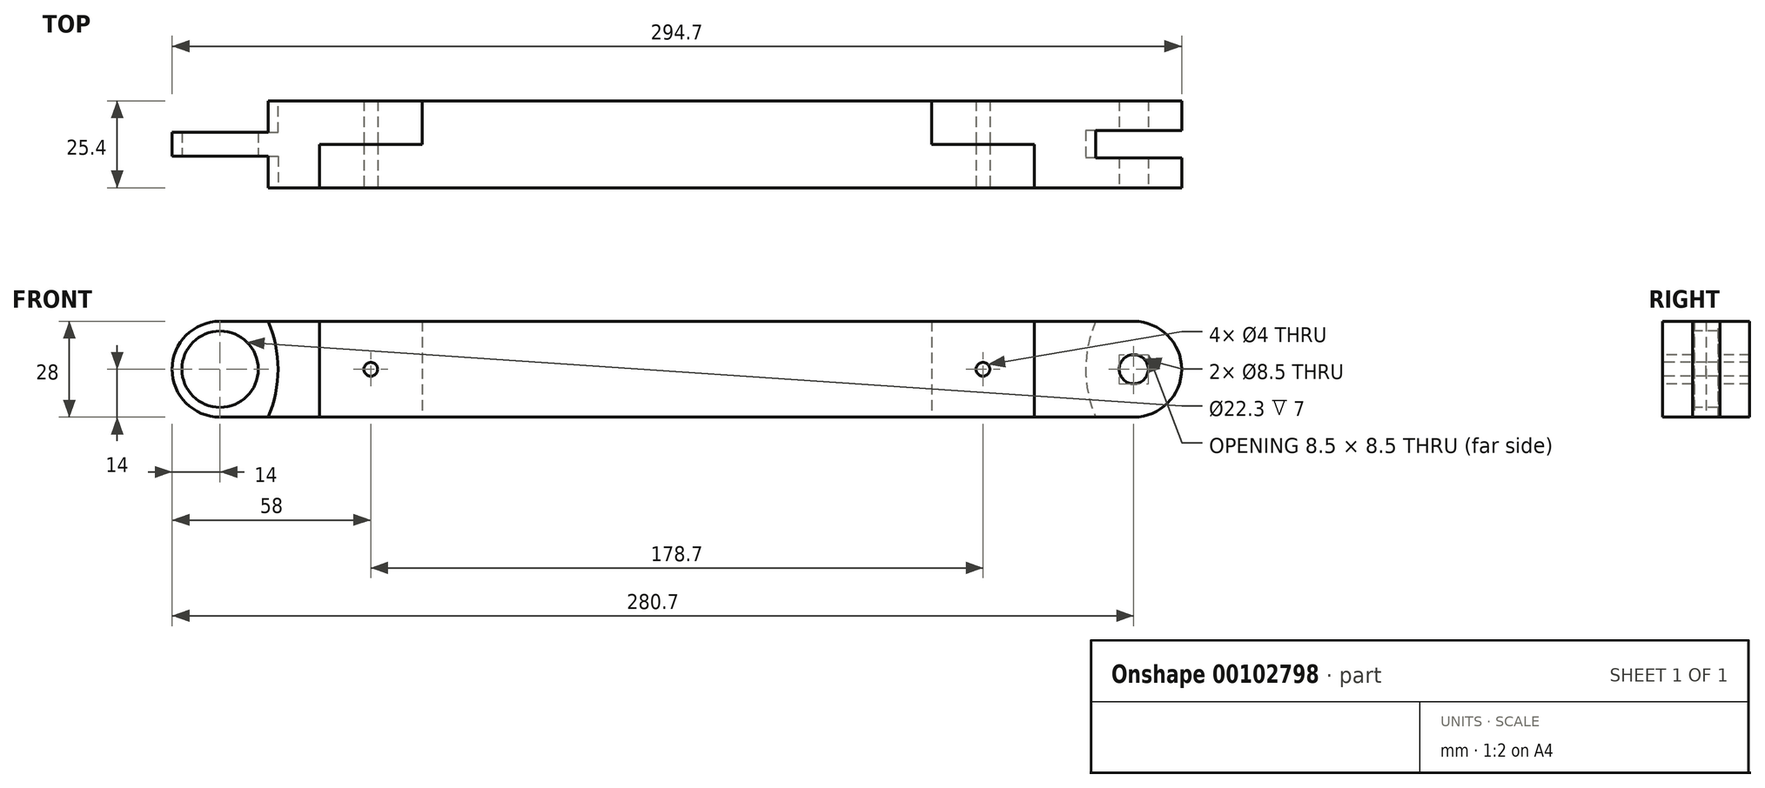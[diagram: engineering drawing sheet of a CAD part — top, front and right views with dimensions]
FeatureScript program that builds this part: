
annotation { "Feature Type Name" : "Feature", "Feature Type Description" : "" }
export const myFeature = defineFeature(function(context is Context, id is Id, definition is map)
    precondition{}
    {
        {
            assignVariable(context, id + "F0", {"name" : "diameter", "anyValue" : 28});
        }
        {
            var Q0;
            Q0=qCreatedBy(makeId("Top.planeOp"),FACE);
            var sketch = newSketch(context, id + "F1", { "sketchPlane" : qUnion([Q0])});
            skLineSegment(sketch, "E0", {"start": v(-133.35, 12.7) * mm, "end": v(133.35, 12.7) * mm});
            skLineSegment(sketch, "E1", {"start": v(133.35, 12.7) * mm, "end": v(133.35, 4) * mm});
            skLineSegment(sketch, "E2", {"start": v(133.35, 4) * mm, "end": v(105.35, 4) * mm});
            skLineSegment(sketch, "E3", {"start": v(105.35, 4) * mm, "end": v(105.35, -4) * mm});
            skLineSegment(sketch, "E4", {"start": v(105.35, -4) * mm, "end": v(133.35, -4) * mm});
            skLineSegment(sketch, "E5", {"start": v(133.35, -4) * mm, "end": v(133.35, -12.7) * mm});
            skLineSegment(sketch, "E6", {"start": v(133.35, -12.7) * mm, "end": v(-133.35, -12.7) * mm});
            skLineSegment(sketch, "E7", {"start": v(-133.35, -12.7) * mm, "end": v(-133.35, -3.5) * mm});
            skLineSegment(sketch, "E8", {"start": v(-133.35, -3.5) * mm, "end": v(-161.35, -3.5) * mm});
            skLineSegment(sketch, "E9", {"start": v(-161.35, -3.5) * mm, "end": v(-161.35, 3.5) * mm});
            skLineSegment(sketch, "E10", {"start": v(-161.35, 3.5) * mm, "end": v(-133.35, 3.5) * mm});
            skLineSegment(sketch, "E11", {"start": v(-133.35, 3.5) * mm, "end": v(-133.35, 12.7) * mm});
            skPoint(sketch, "E12", {"position": v(-147.35, 0) * mm});
            skPoint(sketch, "E12.positionSnap0", {"position": v(-161.35, 0) * mm});
            skPoint(sketch, "E12.positionSnap1", {"position": v(-147.35, 3.5) * mm});
            skPoint(sketch, "E13", {"position": v(119.35, 0) * mm});
            skPoint(sketch, "E13.positionSnap0", {"position": v(105.35, 0) * mm});
            skPoint(sketch, "E13.positionSnap1", {"position": v(119.35, 4) * mm});
            skPoint(sketch, "E14", {"position": v(0, 0) * mm});
            skPoint(sketch, "E14.positionSnap0", {"position": v(0, 12.7) * mm});
            skLineSegment(sketch, "E15", {"start": v(-118.35, -12.7) * mm, "end": v(-118.35, 0) * mm});
            skLineSegment(sketch, "E16", {"start": v(-118.35, 0) * mm, "end": v(-88.35, 0) * mm});
            skLineSegment(sketch, "E17", {"start": v(-88.35, 0) * mm, "end": v(-88.35, 12.7) * mm});
            skLineSegment(sketch, "E18", {"start": v(0, 12.7) * mm, "end": v(0, -12.7) * mm, "construction": true});
            skLineSegment(sketch, "E19", {"start": v(90.35, -12.7) * mm, "end": v(90.35, 0) * mm});
            skLineSegment(sketch, "E20", {"start": v(90.35, 0) * mm, "end": v(60.35, 0) * mm});
            skLineSegment(sketch, "E21", {"start": v(60.35, 0) * mm, "end": v(60.35, 12.7) * mm});
            skLineSegment(sketch, "E22", {"start": v(-133.35, -8.1) * mm, "end": v(-118.35, -8.1) * mm, "construction": true});
            skLineSegment(sketch, "E23", {"start": v(90.35, 0) * mm, "end": v(105.35, 0) * mm, "construction": true});
            skSolve(sketch);
        }
        {
            var Q0;
            {var subQ1=sQuery(id+"F1.wireOp",EDGE,"E7");Q0=makeQuery(id+"F1.imprint","IMPRINT",FACE,{"disambiguationData":[TD([[makeQuery(id+"F1.imprint","IMPRINT",EDGE,{"derivedFrom":subQ1}),-1.0]])]});}
            extrude(context, id + "F2", {"entities" : qUnion([Q0]), "depth" : (getVariable(context, 'diameter')) * mm});
        }
        {
            var Q0;
            {var subQ0=sQuery(id+"F1.wireOp",EDGE,"E15");Q0=makeQuery(id+"F1.imprint","IMPRINT",FACE,{"disambiguationData":[TD([[makeQuery(id+"F1.imprint","IMPRINT",EDGE,{"derivedFrom":subQ0}),-1.0]])]});}
            var Q1;
            Q1=makeQuery(id+"F2.opExtrude","CAP_FACE",FACE,{"disambiguationData":[OSD([sQuery(id+"F1.wireOp",EDGE,"E0"),sQuery(id+"F1.wireOp",EDGE,"E6"),sQuery(id+"F1.wireOp",EDGE,"E7"),sQuery(id+"F1.wireOp",EDGE,"E8"),sQuery(id+"F1.wireOp",EDGE,"E9"),sQuery(id+"F1.wireOp",EDGE,"E10"),sQuery(id+"F1.wireOp",EDGE,"E11"),sQuery(id+"F1.wireOp",EDGE,"E15"),sQuery(id+"F1.wireOp",EDGE,"E16"),sQuery(id+"F1.wireOp",EDGE,"E17")])],"isStart":false});
            extrude(context, id + "F3", {"entities" : qUnion([Q0]), "endBound" : BoundingType.UP_TO_SURFACE, "endBoundEntityFace" : qUnion([Q1]), "depth" : 25 * mm});
        }
        {
            var Q0;
            {var subQ0=sQuery(id+"F1.wireOp",EDGE,"E1");Q0=makeQuery(id+"F1.imprint","IMPRINT",FACE,{"disambiguationData":[TD([[makeQuery(id+"F1.imprint","IMPRINT",EDGE,{"derivedFrom":subQ0}),-1.0]])]});}
            var Q1;
            Q1=makeQuery(id+"F2.opExtrude","CAP_FACE",FACE,{"disambiguationData":[OSD([sQuery(id+"F1.wireOp",EDGE,"E0"),sQuery(id+"F1.wireOp",EDGE,"E6"),sQuery(id+"F1.wireOp",EDGE,"E7"),sQuery(id+"F1.wireOp",EDGE,"E8"),sQuery(id+"F1.wireOp",EDGE,"E9"),sQuery(id+"F1.wireOp",EDGE,"E10"),sQuery(id+"F1.wireOp",EDGE,"E11"),sQuery(id+"F1.wireOp",EDGE,"E15"),sQuery(id+"F1.wireOp",EDGE,"E16"),sQuery(id+"F1.wireOp",EDGE,"E17")])],"isStart":false});
            extrude(context, id + "F4", {"entities" : qUnion([Q0]), "endBound" : BoundingType.UP_TO_SURFACE, "endBoundEntityFace" : qUnion([Q1]), "depth" : 25 * mm});
        }
        {
            var Q0;
            Q0=makeQuery(id+"F3.opExtrude","SWEPT_FACE",FACE,{"disambiguationData":[OSD([sQuery(id+"F1.wireOp",EDGE,"E6")])]});
            var sketch = newSketch(context, id + "F5", { "sketchPlane" : qUnion([Q0])});
            skLineSegment(sketch, "E24.0.0", {"start": v(-161.35, 0) * mm, "end": v(-133.35, 0) * mm});
            skLineSegment(sketch, "E24.0.1", {"start": v(-133.35, 0) * mm, "end": v(-133.35, 28) * mm});
            skLineSegment(sketch, "E24.0.2", {"start": v(-133.35, 28) * mm, "end": v(-161.35, 28) * mm});
            skLineSegment(sketch, "E24.0.3", {"start": v(-161.35, 28) * mm, "end": v(-161.35, 0) * mm});
            skLineSegment(sketch, "E25.0.0", {"start": v(105.35, 0) * mm, "end": v(105.35, 28) * mm});
            skLineSegment(sketch, "E25.0.1", {"start": v(105.35, 28) * mm, "end": v(133.35, 28) * mm});
            skLineSegment(sketch, "E25.0.2", {"start": v(133.35, 28) * mm, "end": v(133.35, 0) * mm});
            skLineSegment(sketch, "E25.0.3", {"start": v(133.35, 0) * mm, "end": v(105.35, 0) * mm});
            skCircle(sketch, "E26", {"center": v(119.35, 14) * mm, "radius": 4.25 * mm});
            skPoint(sketch, "E26.centerSnap0", {"position": v(133.35, 14) * mm});
            skPoint(sketch, "E26.centerSnap1", {"position": v(119.35, 28) * mm});
            skArc(sketch, "E27", {"start": v(119.35, 28) * mm, "mid": v(133.35, 14) * mm, "end": v(119.35, 0) * mm});
            skArc(sketch, "E28", {"start": v(108.27, 28) * mm, "mid": v(105.35, 14) * mm, "end": v(108.27, 0) * mm});
            skCircle(sketch, "E29", {"center": v(-147.35, 14) * mm, "radius": 11.15 * mm});
            skPoint(sketch, "E29.centerSnap0", {"position": v(-161.35, 14) * mm});
            skPoint(sketch, "E29.centerSnap1", {"position": v(-147.35, 28) * mm});
            skArc(sketch, "E30", {"start": v(-147.35, 28) * mm, "mid": v(-161.35, 14) * mm, "end": v(-147.35, 0) * mm});
            skArc(sketch, "E31", {"start": v(-133.35, 28) * mm, "mid": v(-130.43, 14) * mm, "end": v(-133.35, 0) * mm});
            skSolve(sketch);
        }
        {
            var Q0;
            Q0=makeQuery(id+"F5.imprint","IMPRINT",FACE,{"disambiguationData":[TD([[makeQuery(id+"F5.imprint","IMPRINT",EDGE,{"derivedFrom":sQuery(id+"F5.wireOp",EDGE,"E29")}),1.0]])]});
            var Q1;
            {var subQ0=sQuery(id+"F5.wireOp",EDGE,"E24.0.3");var subQ1=sQuery(id+"F5.wireOp",EDGE,"E24.0.2");var subQ2=makeQuery(id+"F5.imprint","INTERSECT",VERTEX,{"derivedFrom":[subQ1,subQ0]});Q1=makeQuery(id+"F5.imprint","IMPRINT",FACE,{"disambiguationData":[TD([[makeQuery(id+"F5.imprint","IMPRINT",EDGE,{"disambiguationData":[TD([[subQ2,1.0]])],"derivedFrom":subQ1}),1.0]])]});}
            var Q2;
            {var subQ0=sQuery(id+"F5.wireOp",EDGE,"E24.0.3");var subQ1=sQuery(id+"F5.wireOp",EDGE,"E24.0.0");var subQ2=makeQuery(id+"F5.imprint","INTERSECT",VERTEX,{"derivedFrom":[subQ1,subQ0]});Q2=makeQuery(id+"F5.imprint","IMPRINT",FACE,{"disambiguationData":[TD([[makeQuery(id+"F5.imprint","IMPRINT",EDGE,{"disambiguationData":[TD([[subQ2,-1.0]])],"derivedFrom":subQ1}),1.0]])]});}
            var Q3;
            Q3=makeQuery(id+"F2.opExtrude","SWEPT_FACE",FACE,{"disambiguationData":[OSD([sQuery(id+"F1.wireOp",EDGE,"E10")])]});
            extrude(context, id + "F6", {"entities" : qUnion([Q0, Q1, Q2]), "operationType" : NewBodyOperationType.REMOVE, "endBound" : BoundingType.UP_TO_SURFACE, "oppositeDirection" : true, "endBoundEntityFace" : qUnion([Q3]), "depth" : 25 * mm});
        }
        {
            var Q0;
            Q0=makeQuery(id+"F5.imprint","IMPRINT",FACE,{"disambiguationData":[TD([[makeQuery(id+"F5.imprint","IMPRINT",EDGE,{"derivedFrom":sQuery(id+"F5.wireOp",EDGE,"E26")}),1.0]])]});
            var Q1;
            {var subQ0=sQuery(id+"F5.wireOp",EDGE,"E25.0.2");var subQ1=sQuery(id+"F5.wireOp",EDGE,"E25.0.1");var subQ2=makeQuery(id+"F5.imprint","INTERSECT",VERTEX,{"derivedFrom":[subQ1,subQ0]});Q1=makeQuery(id+"F5.imprint","IMPRINT",FACE,{"disambiguationData":[TD([[makeQuery(id+"F5.imprint","IMPRINT",EDGE,{"disambiguationData":[TD([[subQ2,1.0]])],"derivedFrom":subQ1}),-1.0]])]});}
            var Q2;
            {var subQ0=sQuery(id+"F5.wireOp",EDGE,"E25.0.3");var subQ1=sQuery(id+"F5.wireOp",EDGE,"E25.0.2");var subQ2=makeQuery(id+"F5.imprint","INTERSECT",VERTEX,{"derivedFrom":[subQ1,subQ0]});Q2=makeQuery(id+"F5.imprint","IMPRINT",FACE,{"disambiguationData":[TD([[makeQuery(id+"F5.imprint","IMPRINT",EDGE,{"disambiguationData":[TD([[subQ2,1.0]])],"derivedFrom":subQ1}),-1.0]])]});}
            var Q3;
            Q3=makeQuery(id+"F4.opExtrude","SWEPT_FACE",FACE,{"disambiguationData":[OSD([sQuery(id+"F1.wireOp",EDGE,"E0")])]});
            extrude(context, id + "F7", {"entities" : qUnion([Q0, Q1, Q2]), "operationType" : NewBodyOperationType.REMOVE, "endBound" : BoundingType.UP_TO_SURFACE, "oppositeDirection" : true, "endBoundEntityFace" : qUnion([Q3]), "depth" : 25 * mm});
        }
        {
            var Q0;
            {var subQ0=sQuery(id+"F5.wireOp",EDGE,"E25.0.1");var subQ1=sQuery(id+"F5.wireOp",EDGE,"E25.0.0");var subQ2=makeQuery(id+"F5.imprint","INTERSECT",VERTEX,{"derivedFrom":[subQ1,subQ0]});Q0=makeQuery(id+"F5.imprint","IMPRINT",FACE,{"disambiguationData":[TD([[makeQuery(id+"F5.imprint","IMPRINT",EDGE,{"disambiguationData":[TD([[subQ2,1.0]])],"derivedFrom":subQ1}),-1.0]])]});}
            var Q1;
            {var subQ0=sQuery(id+"F5.wireOp",EDGE,"E25.0.3");var subQ1=sQuery(id+"F5.wireOp",EDGE,"E25.0.0");var subQ2=makeQuery(id+"F5.imprint","INTERSECT",VERTEX,{"derivedFrom":[subQ1,subQ0]});Q1=makeQuery(id+"F5.imprint","IMPRINT",FACE,{"disambiguationData":[TD([[makeQuery(id+"F5.imprint","IMPRINT",EDGE,{"disambiguationData":[TD([[subQ2,-1.0]])],"derivedFrom":subQ1}),-1.0]])]});}
            var Q2;
            Q2=makeQuery(id+"F4.opExtrude","SWEPT_FACE",FACE,{"disambiguationData":[OSD([sQuery(id+"F1.wireOp",EDGE,"E2")])]});
            extrude(context, id + "F8", {"entities" : qUnion([Q0, Q1]), "operationType" : NewBodyOperationType.ADD, "endBound" : BoundingType.UP_TO_SURFACE, "oppositeDirection" : true, "endBoundEntityFace" : qUnion([Q2]), "depth" : 25 * mm});
        }
        {
            var Q0;
            Q0=makeQuery(id+"F5.imprint","IMPRINT",FACE,{"disambiguationData":[TD([[makeQuery(id+"F5.imprint","IMPRINT",EDGE,{"derivedFrom":sQuery(id+"F5.wireOp",EDGE,"E24.0.1")}),-1.0]])]});
            var Q1;
            Q1=makeQuery(id+"F2.opExtrude","SWEPT_FACE",FACE,{"disambiguationData":[OSD([sQuery(id+"F1.wireOp",EDGE,"E8")])]});
            extrude(context, id + "F9", {"entities" : qUnion([Q0]), "endBound" : BoundingType.UP_TO_SURFACE, "oppositeDirection" : true, "endBoundEntityFace" : qUnion([Q1]), "depth" : 25 * mm});
        }
        {
            var Q0;
            Q0=makeQuery(id+"F9.opExtrude","SWEPT_BODY",BODY,{"disambiguationData":[OSD([sQuery(id+"F5.wireOp",EDGE,"E24.0.1"),sQuery(id+"F5.wireOp",EDGE,"E31")])]});
            var Q1;
            Q1=qCreatedBy(makeId("Front.planeOp"),FACE);
            mirror(context, id + "F10", {"operationType" : NewBodyOperationType.REMOVE, "entities" : qUnion([Q0]), "mirrorPlane" : qUnion([Q1])});
        }
        {
            var Q0;
            Q0=makeQuery(id+"F9.opExtrude","SWEPT_BODY",BODY,{"disambiguationData":[OSD([sQuery(id+"F5.wireOp",EDGE,"E24.0.1"),sQuery(id+"F5.wireOp",EDGE,"E31")])]});
            var Q1;
            Q1=makeQuery(id+"F2.opExtrude","SWEPT_BODY",BODY,{"disambiguationData":[OSD([sQuery(id+"F1.wireOp",EDGE,"E0"),sQuery(id+"F1.wireOp",EDGE,"E6"),sQuery(id+"F1.wireOp",EDGE,"E7"),sQuery(id+"F1.wireOp",EDGE,"E8"),sQuery(id+"F1.wireOp",EDGE,"E9"),sQuery(id+"F1.wireOp",EDGE,"E10"),sQuery(id+"F1.wireOp",EDGE,"E11"),sQuery(id+"F1.wireOp",EDGE,"E15"),sQuery(id+"F1.wireOp",EDGE,"E16"),sQuery(id+"F1.wireOp",EDGE,"E17")])]});
            booleanBodies(context, id + "F11", {"operationType" : BooleanOperationType.SUBTRACTION, "tools" : qUnion([Q0]), "targets" : qUnion([Q1])});
        }
        {
            var Q0;
            Q0=makeQuery(id+"F3.opExtrude","SWEPT_FACE",FACE,{"disambiguationData":[OSD([sQuery(id+"F1.wireOp",EDGE,"E6")])]});
            var sketch = newSketch(context, id + "F12", { "sketchPlane" : qUnion([Q0])});
            skLineSegment(sketch, "E32.0.0", {"start": v(90.35, 0) * mm, "end": v(90.35, 28) * mm});
            skLineSegment(sketch, "E32.0.1", {"start": v(90.35, 28) * mm, "end": v(60.35, 28) * mm});
            skLineSegment(sketch, "E32.0.2", {"start": v(60.35, 28) * mm, "end": v(60.35, 0) * mm});
            skLineSegment(sketch, "E32.0.3", {"start": v(60.35, 0) * mm, "end": v(90.35, 0) * mm});
            skLineSegment(sketch, "E33.0.0", {"start": v(-118.35, 0) * mm, "end": v(-88.35, 0) * mm});
            skLineSegment(sketch, "E33.0.1", {"start": v(-88.35, 0) * mm, "end": v(-88.35, 28) * mm});
            skLineSegment(sketch, "E33.0.2", {"start": v(-88.35, 28) * mm, "end": v(-118.35, 28) * mm});
            skLineSegment(sketch, "E33.0.3", {"start": v(-118.35, 28) * mm, "end": v(-118.35, 0) * mm});
            skCircle(sketch, "E34", {"center": v(-103.35, 14) * mm, "radius": 2 * mm});
            skPoint(sketch, "E34.centerSnap0", {"position": v(-103.35, 28) * mm});
            skPoint(sketch, "E34.centerSnap1", {"position": v(-118.35, 14) * mm});
            skCircle(sketch, "E35", {"center": v(75.35, 14) * mm, "radius": 2 * mm});
            skPoint(sketch, "E35.centerSnap0", {"position": v(90.35, 14) * mm});
            skPoint(sketch, "E35.centerSnap1", {"position": v(75.35, 28) * mm});
            skSolve(sketch);
        }
        {
            var Q0;
            Q0=makeQuery(id+"F12.imprint","IMPRINT",FACE,{"disambiguationData":[TD([[makeQuery(id+"F12.imprint","IMPRINT",EDGE,{"derivedFrom":sQuery(id+"F12.wireOp",EDGE,"E34")}),1.0]])]});
            var Q1;
            Q1=makeQuery(id+"F12.imprint","IMPRINT",FACE,{"disambiguationData":[TD([[makeQuery(id+"F12.imprint","IMPRINT",EDGE,{"derivedFrom":sQuery(id+"F12.wireOp",EDGE,"E35")}),1.0]])]});
            var Q2;
            Q2=makeQuery(id+"F3.opExtrude","SWEPT_FACE",FACE,{"disambiguationData":[OSD([sQuery(id+"F1.wireOp",EDGE,"E0")])]});
            extrude(context, id + "F13", {"entities" : qUnion([Q0, Q1]), "operationType" : NewBodyOperationType.REMOVE, "endBound" : BoundingType.UP_TO_SURFACE, "oppositeDirection" : true, "endBoundEntityFace" : qUnion([Q2]), "depth" : 25 * mm});
        }
    });
